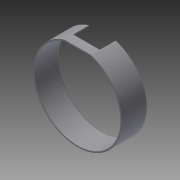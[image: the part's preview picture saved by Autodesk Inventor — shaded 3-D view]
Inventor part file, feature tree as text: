
AUTODESK INVENTOR PART (.ipt)
format: ipt  version: 2015 (Build 190159000, 159)  size: 117,760 bytes
history: native  units: mm
features: extrude x4, sketch x4, fillet x1
ambient origin geometry x8: Origin, YZ Plane, XZ Plane, XY Plane, X Axis, Y Axis, Z Axis, Center Point
bodies: Solid1 (feature_tree)
feature tree (9):
  extrude  "Extrusion1"  Depth=97.0mm
  extrude  "Extrusion2"  Depth=10.0mm
  extrude  "Extrusion3"  Depth=10.0mm TaperAngle=0.0deg
  extrude  "Extrusion4"  Depth=2.0mm
  fillet  "Fillet1"  Radius=30.0mm
  sketch  "Sketch1"  dims[d0=100.0mm d1=97.0mm]
  sketch  "Sketch2"  dims[d2=30.0mm d3=0.0mm d4=10.0mm]
  sketch  "Sketch3"  dims[d5=10.0mm d6=10.0mm d7=0.0mm]
  sketch  "Sketch4"  dims[d8=15.0mm d9=15.0mm d10=30.0mm d11=0.0mm d12=10.0mm d13=0.0mm d14=2.0mm]
